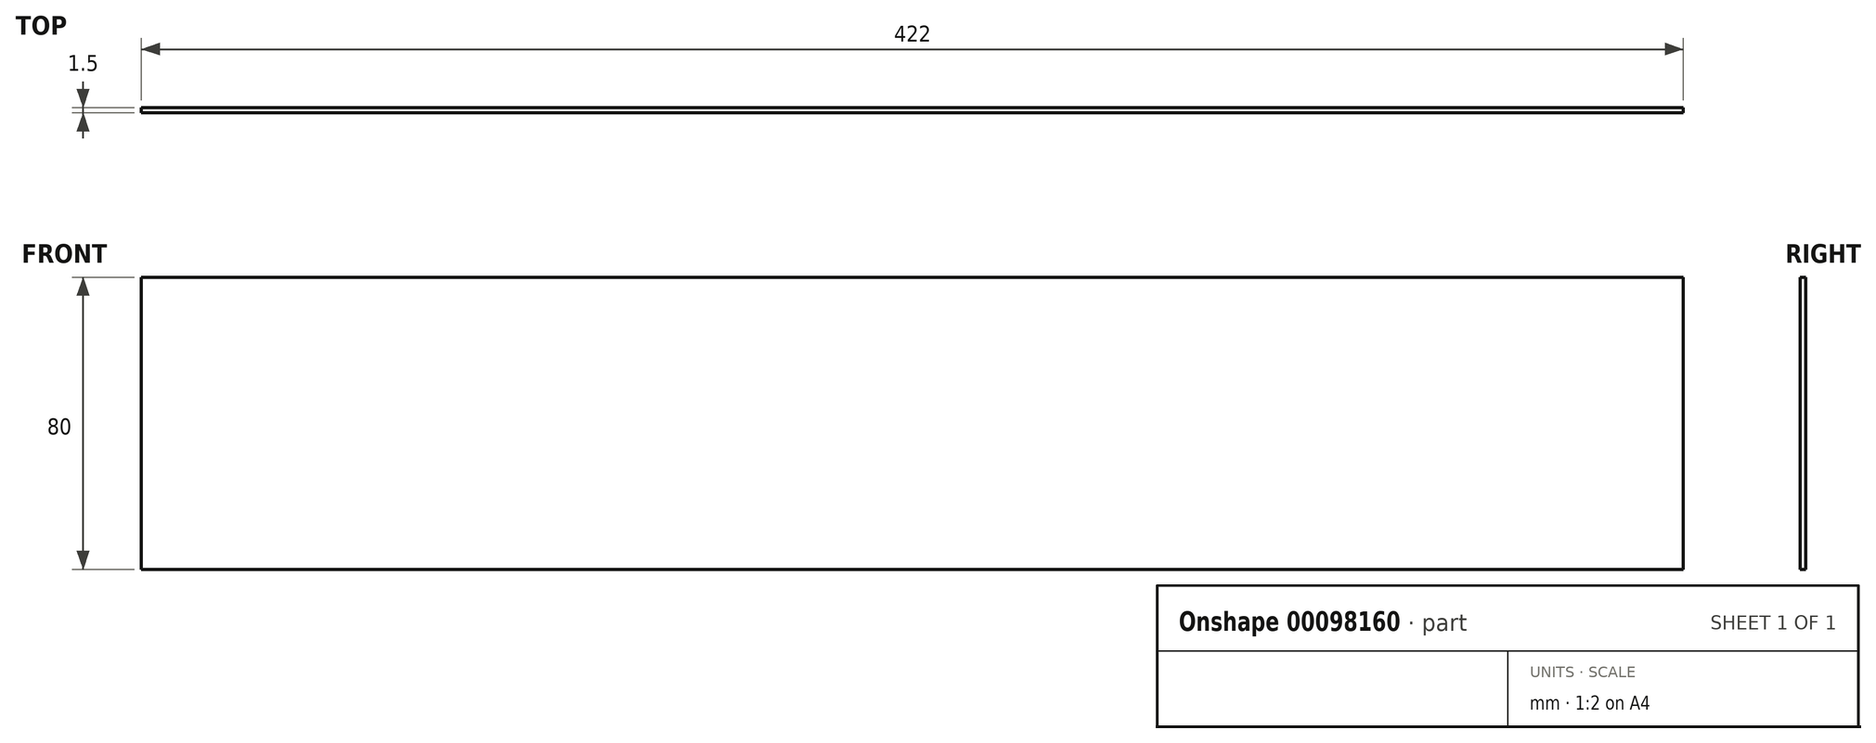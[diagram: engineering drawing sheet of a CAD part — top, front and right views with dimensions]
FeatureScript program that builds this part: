
annotation { "Feature Type Name" : "Feature", "Feature Type Description" : "" }
export const myFeature = defineFeature(function(context is Context, id is Id, definition is map)
    precondition{}
    {
        {
            var Q0;
            Q0=qCreatedBy(makeId("Front.planeOp"),FACE);
            var sketch = newSketch(context, id + "F0", { "sketchPlane" : qUnion([Q0])});
            skLineSegment(sketch, "E0.bottom", {"start": v(-279.84, -24.11) * mm, "end": v(142.16, -24.11) * mm});
            skLineSegment(sketch, "E0.top", {"start": v(-279.84, -104.11) * mm, "end": v(142.16, -104.11) * mm});
            skLineSegment(sketch, "E0.left", {"start": v(-279.84, -24.11) * mm, "end": v(-279.84, -104.11) * mm});
            skLineSegment(sketch, "E0.right", {"start": v(142.16, -24.11) * mm, "end": v(142.16, -104.11) * mm});
            skSolve(sketch);
        }
        {
            var Q0;
            Q0=makeQuery(id+"F0.imprint","IMPRINT",FACE,{"disambiguationData":[TD([[makeQuery(id+"F0.imprint","IMPRINT",EDGE,{"derivedFrom":sQuery(id+"F0.wireOp",EDGE,"E0.bottom")}),-1.0]])]});
            extrude(context, id + "F1", {"entities" : qUnion([Q0]), "depth" : 1.5 * mm});
        }
    });
